# Revit family: Gira_029003
name_source: partatom
category: Elektroinstallationen
revit_build: Autodesk Revit 2017 (Build: 20160225_1515(x64)
units: mm (PartAtom-declared; Revit-internal decimal feet)

## family parameters
Basisbauteil = Fläche
Beim Laden mit Abzugskörper schneiden = Nein
Bemaßung runder Anschluss = Durchmesser verwenden
Beschriftungsausrichtung beibehalten = Nein
Gemeinsam genutzt = Nein
Raumberechnungspunkt = Nein
Teiletyp = Normal

## types (1)
- Gira_029003
    Abtastbares Symbol/barrierefrei = Nein
    Andere Bussysteme = ohne
    Anschluss = Zweidraht
    Art der Spannungsversorgung = 230 V AC
    Aufdruck/Kennzeichnung = ohne Aufdruck
    Ausführung = einteilige Wippe
    Ausführung Aufnehmer/Fühler = sonstige
    Ausführung der Oberfläche = glänzend
    BIM = https://media.stage.bim.site und Tasten.rfa
    Bauelement = Sys55_Abdeckung_Schalten und Tasten
    Bedienung = Dreh
    Befestigungsart = Klemmbefestigung
    Beschreibung = Wippe mit Kontrollfenster  Reinweiß glänzend
    Beschriftungsfeld = ohne Beschriftungsfeld
    Bussystem Funkbus = Nein
    Bussystem KNX = Ja
    Bussystem KNX-Funk = Nein
    Bussystem LON = Nein
    Bussystem Powernet = Nein
    Datenblatt = https://katalog.gira.de
    Differenz verstellbar = Nein
    Explosionsgeschützt = Nein
    Farbe = weiß
    GTIN = 4010337290032
    Geeignet für Bussystem-Tasterankopplung = Nein
    Geeignet für Schutzart (IP) = IP20
    HAN = 029003
    Halogenfrei = Ja
    Heizen = Ja
    Hersteller = Gira
    Kontrollfenster/Lichtauslass = Ja
    Kühlen = Nein
    Lüsterklemme = Nein
    Messbereich oberer Wert [m/s] = 30
    Messbereich unterer Wert [m/s] = 5
    Mit Aufdruck = Nein
    Mit Beschriftungsfeld = Nein
    Mit Display = Nein
    Mit Empfänger = Nein
    Mit Geräuschniveauanzeige = Nein
    Mit Klappdeckel = Nein
    Mit Staubschutz = Nein
    Mit Trinkwasserschaltung = Nein
    Mit Zugentlastung = Nein
    Mit austauschbarer Linse/Symbol = Nein
    Montageart = Unterputz
    Oberfläche = sonstige
    Produktseite = http://katalog.gira.de
    RAL-Nummer = 9010
    RAL-Nummer (ähnlich) = 9010
    Regelcharakteristik = sonstige
    Schutzart (IP) = IP20
    Sensor extern = Nein
    Temperatur ablesbar = Nein
    Thermische Rückkopplung = ohne
    Tragring = Nein
    Transparent = Nein
    Typ Kontakt = Öffner
    Typname = Abd. Knopf Dimmer + Potentiometer System 55 Reinweiß
    URL = https://www.gira.de
    Verwendung = Schalter/Taster
    Vorgabe-Ansicht = 1219 mm
    Werkstoff = Kunststoff
    Werkstoffgüte = Thermoplast
    Zusammenstellung = Zentralplatte

## geometry (parser evidence)
native form markers: Sweep x7
no freeform markers — native parametric forms only
